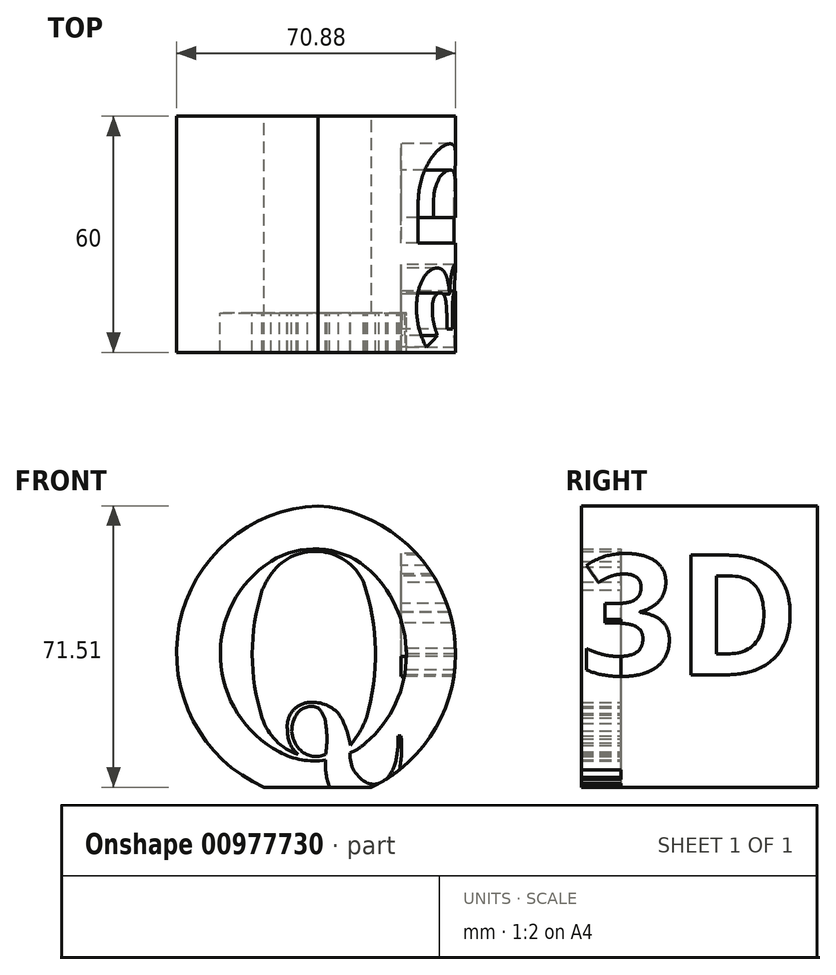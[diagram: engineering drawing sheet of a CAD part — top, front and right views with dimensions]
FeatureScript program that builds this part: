
annotation { "Feature Type Name" : "Feature", "Feature Type Description" : "" }
export const myFeature = defineFeature(function(context is Context, id is Id, definition is map)
    precondition{}
    {
        {
            var Q0;
            Q0=qCreatedBy(makeId("Front.planeOp"),FACE);
            var sketch = newSketch(context, id + "F0", { "sketchPlane" : qUnion([Q0])});
            skPoint(sketch, "E0.first.point", {"position": v(-8.97, 42.4) * mm});
            skPoint(sketch, "E0.second.point", {"position": v(4.84, -31.38) * mm});
            skPoint(sketch, "E0.third.point", {"position": v(40.23, 13.72) * mm});
            skArc(sketch, "E1", {"start": v(0, 43.7) * mm, "mid": v(-36.34, 3.66) * mm, "end": v(4.84, -31.38) * mm});
            skArc(sketch, "E2", {"start": v(20.57, -24) * mm, "mid": v(33.91, 17.02) * mm, "end": v(0, 43.7) * mm});
            skArc(sketch, "E3", {"start": v(-12, 29.47) * mm, "mid": v(-24.84, 4.65) * mm, "end": v(-9.87, -18.96) * mm});
            skArc(sketch, "E4", {"start": v(12.09, 28.05) * mm, "mid": v(0.27, 32.56) * mm, "end": v(-12, 29.47) * mm});
            skArc(sketch, "E5", {"start": v(12.09, -16.68) * mm, "mid": v(22.4, 5.68) * mm, "end": v(12.09, 28.05) * mm});
            skArc(sketch, "E6", {"start": v(8.11, -19.25) * mm, "mid": v(10.22, -18.15) * mm, "end": v(12.09, -16.68) * mm});
            skArc(sketch, "E7", {"start": v(-9.87, -18.96) * mm, "mid": v(-4.16, -21) * mm, "end": v(1.9, -21.05) * mm});
            skArc(sketch, "E8", {"start": v(1.9, -21.05) * mm, "mid": v(2.44, -26.48) * mm, "end": v(4.84, -31.38) * mm});
            skArc(sketch, "E9", {"start": v(8.11, -19.25) * mm, "mid": v(9.16, -23.77) * mm, "end": v(12.57, -26.92) * mm});
            skArc(sketch, "E10", {"start": v(12.57, -26.92) * mm, "mid": v(15.38, -27) * mm, "end": v(17.7, -25.42) * mm});
            skArc(sketch, "E11", {"start": v(17.7, -25.42) * mm, "mid": v(19.27, -22.75) * mm, "end": v(19.99, -19.74) * mm});
            skArc(sketch, "E12", {"start": v(19.99, -19.74) * mm, "mid": v(20.3, -17.3) * mm, "end": v(20.33, -14.85) * mm});
            skLineSegment(sketch, "E13", {"start": v(20.33, -14.85) * mm, "end": v(21.05, -14.85) * mm});
            skArc(sketch, "E14", {"start": v(20.57, -24) * mm, "mid": v(21.16, -19.45) * mm, "end": v(21.05, -14.85) * mm});
            skArc(sketch, "E15", {"start": v(11.56, 24.17) * mm, "mid": v(0.05, 31.98) * mm, "end": v(-12.33, 25.65) * mm});
            skArc(sketch, "E16", {"start": v(-12.33, 25.65) * mm, "mid": v(-13.33, 23.93) * mm, "end": v(-14.2, 22.14) * mm});
            skArc(sketch, "E17", {"start": v(12.27, -10.4) * mm, "mid": v(14.51, 6.94) * mm, "end": v(11.56, 24.17) * mm});
            skArc(sketch, "E18", {"start": v(8.2, -17.28) * mm, "mid": v(10.48, -13.99) * mm, "end": v(12.27, -10.4) * mm});
            skArc(sketch, "E19", {"start": v(-14.2, 22.14) * mm, "mid": v(-16.74, 5.87) * mm, "end": v(-14.2, -10.4) * mm});
            skArc(sketch, "E20", {"start": v(-14.2, -10.4) * mm, "mid": v(-10.74, -16.1) * mm, "end": v(-5.08, -19.62) * mm});
            skArc(sketch, "E21.trimOffspring", {"start": v(21.12, -15.68) * mm, "mid": v(21.07, -15.26) * mm, "end": v(21.03, -14.85) * mm});
            skArc(sketch, "E22", {"start": v(-7.75, -13.7) * mm, "mid": v(-7.09, -16.96) * mm, "end": v(-5.08, -19.62) * mm});
            skArc(sketch, "E23", {"start": v(-2.67, -6.43) * mm, "mid": v(-6.77, -8.98) * mm, "end": v(-7.75, -13.7) * mm});
            skArc(sketch, "E24", {"start": v(5.17, -9.2) * mm, "mid": v(1.57, -6.89) * mm, "end": v(-2.67, -6.43) * mm});
            skArc(sketch, "E25", {"start": v(8.2, -17.28) * mm, "mid": v(7.13, -13.07) * mm, "end": v(5.17, -9.2) * mm});
            skArc(sketch, "E26", {"start": v(1.9, -19.62) * mm, "mid": v(2.22, -15.67) * mm, "end": v(1.9, -11.72) * mm});
            skArc(sketch, "E27", {"start": v(1.9, -11.72) * mm, "mid": v(1.3, -9.59) * mm, "end": v(0, -7.8) * mm});
            skArc(sketch, "E28", {"start": v(0, -7.8) * mm, "mid": v(-3.12, -7.64) * mm, "end": v(-5.56, -9.59) * mm});
            skPoint(sketch, "E28.endSnap0", {"position": v(1.3, -9.59) * mm});
            skArc(sketch, "E29", {"start": v(-5.56, -9.59) * mm, "mid": v(-6.65, -14.33) * mm, "end": v(-4.4, -18.65) * mm});
            skArc(sketch, "E30", {"start": v(-4.4, -18.65) * mm, "mid": v(-1.39, -20.08) * mm, "end": v(1.9, -19.62) * mm});
            skSolve(sketch);
        }
        {
            var Q0;
            Q0=qSketchRegion(id+"F0",true);
            extrude(context, id + "F1", {"entities" : qUnion([Q0]), "depth" : 25 * mm, "offsetDistance" : 25 * mm});
        }
        {
            var Q0;
            Q0=qCreatedBy(makeId("Front.planeOp"),FACE);
            var sketch = newSketch(context, id + "F2", { "sketchPlane" : qUnion([Q0])});
            skArc(sketch, "E31", {"start": v(0, 43.75) * mm, "mid": v(-36.28, 3.67) * mm, "end": v(4.78, -31.5) * mm});
            skArc(sketch, "E32", {"start": v(4.78, -31.5) * mm, "mid": v(35.24, 8.21) * mm, "end": v(0, 43.75) * mm});
            skSolve(sketch);
        }
        {
            var Q0;
            Q0=qSketchRegion(id+"F2",true);
            extrude(context, id + "F3", {"entities" : qUnion([Q0]), "operationType" : NewBodyOperationType.ADD, "oppositeDirection" : true, "depth" : 35 * mm, "offsetDistance" : 25 * mm});
        }
        {
            var Q0;
            Q0 = qSketchRegion(id + "F2", true);
            extrude(context, id + "F4", {"entities" : qUnion([Q0]), "operationType" : NewBodyOperationType.ADD, "depth" : 15 * mm, "offsetDistance" : 25 * mm, "hasSecondDirection" : true, "secondDirectionOppositeDirection" : true, "secondDirectionDepth" : 25 * mm});
        }
        {
            var Q0;
            Q0=makeQuery(id+"F3.opExtrude","CAP_FACE",FACE,{"disambiguationData":[OSD([sQuery(id+"F2.wireOp",EDGE,"E31"),sQuery(id+"F2.wireOp",EDGE,"E32")])],"isStart":false});
            var sketch = newSketch(context, id + "F5", { "sketchPlane" : qUnion([Q0])});
            skArc(sketch, "E33", {"start": v(0, 43.54) * mm, "mid": v(-34.85, 7.94) * mm, "end": v(-3.9, -31.1) * mm});
            skArc(sketch, "E34", {"start": v(-3.9, -31.1) * mm, "mid": v(35.93, 4.24) * mm, "end": v(0, 43.54) * mm});
            skSolve(sketch);
        }
        {
            var Q0;
            Q0 = qSketchRegion(id + "F5", true);
            extrude(context, id + "F6", {"entities" : qUnion([Q0]), "operationType" : NewBodyOperationType.INTERSECT, "oppositeDirection" : true, "depth" : 109 * mm, "offsetDistance" : 25 * mm});
        }
        {
            var Q0;
            Q0=qCreatedBy(makeId("Right.planeOp"),FACE);
            cPlane(context, id + "F7", {"entities" : qUnion([Q0]), "cplaneType" : CPlaneType.OFFSET, "offset" : 21 * mm, "width" : 150 * mm, "height" : 150 * mm});
        }
        {
            var Q0;
            Q0=qCreatedBy(id+"F7.planeOp",FACE);
            var sketch = newSketch(context, id + "F8", { "sketchPlane" : qUnion([Q0])});
            skText(sketch, "E35", { "text": "3D", "fontName": "OpenSans-Bold.ttf"});
            const initialGuessF8  = {"E35": [-0.02534, 0.00061, 1, 0, 0.03065]};
            skSetInitialGuess(sketch, initialGuessF8);
            skSolve(sketch);
        }
        {
            var Q0;
            Q0 = qSketchRegion(id + "F8", true);
            extrude(context, id + "F9", {"entities" : qUnion([Q0]), "operationType" : NewBodyOperationType.REMOVE, "depth" : 25 * mm, "offsetDistance" : 25 * mm});
        }
        {
            var Q0;
            Q0=makeQuery(id+"F1.opExtrude","CAP_FACE",FACE,{"disambiguationData":[OSD([sQuery(id+"F0.wireOp",EDGE,"E1"),sQuery(id+"F0.wireOp",EDGE,"E2"),sQuery(id+"F0.wireOp",EDGE,"E3"),sQuery(id+"F0.wireOp",EDGE,"E4"),sQuery(id+"F0.wireOp",EDGE,"E5"),sQuery(id+"F0.wireOp",EDGE,"E6"),sQuery(id+"F0.wireOp",EDGE,"E7"),sQuery(id+"F0.wireOp",EDGE,"E8"),sQuery(id+"F0.wireOp",EDGE,"E9"),sQuery(id+"F0.wireOp",EDGE,"E10"),sQuery(id+"F0.wireOp",EDGE,"E11"),sQuery(id+"F0.wireOp",EDGE,"E12"),sQuery(id+"F0.wireOp",EDGE,"E13"),sQuery(id+"F0.wireOp",EDGE,"E14"),sQuery(id+"F0.wireOp",EDGE,"E21.trimOffspring")])],"isStart":false});
            var sketch = newSketch(context, id + "F10", { "sketchPlane" : qUnion([Q0])});
            skLineSegment(sketch, "E36.bottom", {"start": v(-25.73, -36.74) * mm, "end": v(32.4, -36.74) * mm});
            skLineSegment(sketch, "E36.top", {"start": v(-25.73, -27.97) * mm, "end": v(32.4, -27.97) * mm});
            skLineSegment(sketch, "E36.left", {"start": v(-25.73, -36.74) * mm, "end": v(-25.73, -27.97) * mm});
            skLineSegment(sketch, "E36.right", {"start": v(32.4, -36.74) * mm, "end": v(32.4, -27.97) * mm});
            skSolve(sketch);
        }
        {
            var Q0;
            Q0 = qSketchRegion(id + "F10", true);
            extrude(context, id + "F11", {"entities" : qUnion([Q0]), "operationType" : NewBodyOperationType.REMOVE, "oppositeDirection" : true, "depth" : 100 * mm, "offsetDistance" : 25 * mm});
        }
    });
